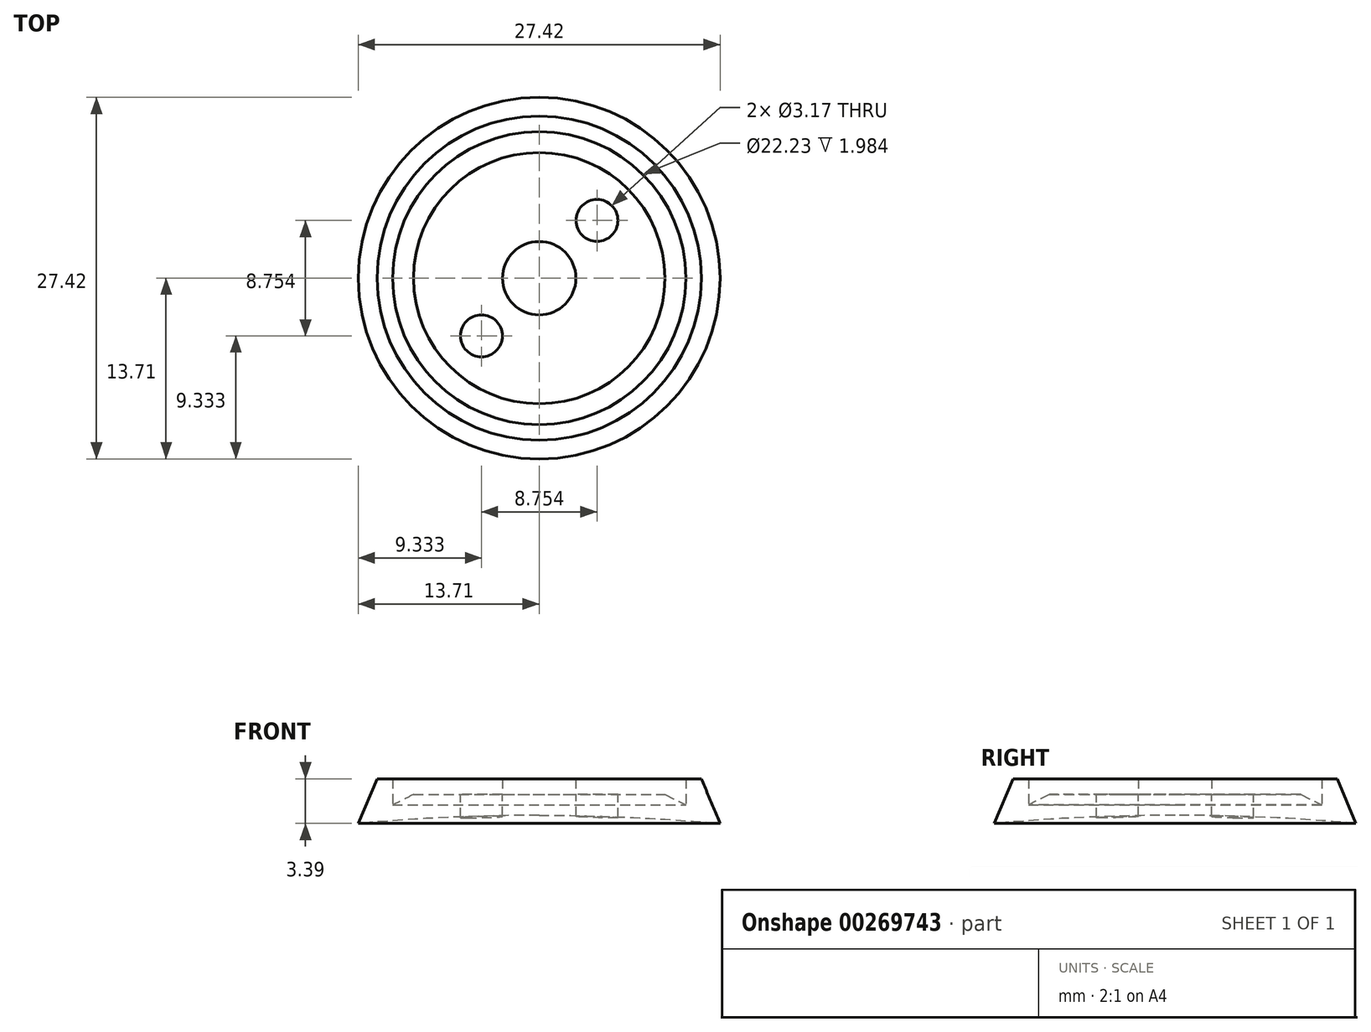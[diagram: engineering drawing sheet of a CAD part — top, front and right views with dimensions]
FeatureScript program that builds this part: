
annotation { "Feature Type Name" : "Feature", "Feature Type Description" : "" }
export const myFeature = defineFeature(function(context is Context, id is Id, definition is map)
    precondition{}
    {
        {
            var Q0;
            Q0=qCreatedBy(makeId("Front.planeOp"),FACE);
            var sketch = newSketch(context, id + "F0", { "sketchPlane" : qUnion([Q0])});
            skArc(sketch, "E0", {"start": v(14.29, 24.73) * mm, "mid": v(7.15, 25.23) * mm, "end": v(0, 25.4) * mm});
            skLineSegment(sketch, "E1", {"start": v(0, 0) * mm, "end": v(0, 65.07) * mm});
            skLineSegment(sketch, "E2", {"start": v(0, 0) * mm, "end": v(11.11, 0) * mm});
            skLineSegment(sketch, "E3", {"start": v(11.11, 0) * mm, "end": v(14.29, 0) * mm});
            skLineSegment(sketch, "E4", {"start": v(14.29, 24.73) * mm, "end": v(14.29, 28.17) * mm});
            skLineSegment(sketch, "E5", {"start": v(14.29, 28.17) * mm, "end": v(11.11, 28.17) * mm});
            skLineSegment(sketch, "E6", {"start": v(2.78, 28.17) * mm, "end": v(0, 28.17) * mm});
            skLineSegment(sketch, "E7", {"start": v(2.78, 28.17) * mm, "end": v(2.78, 26.98) * mm});
            skPoint(sketch, "E8.orphan", {"position": v(11.11, 25) * mm});
            skLineSegment(sketch, "E9", {"start": v(11.11, 26.58) * mm, "end": v(11.11, 28.17) * mm});
            skLineSegment(sketch, "E10", {"start": v(2.78, 26.98) * mm, "end": v(9.53, 26.98) * mm});
            skPoint(sketch, "E11.endSnap0", {"position": v(11.11, 26.58) * mm});
            skLineSegment(sketch, "E12", {"start": v(11.11, 26.58) * mm, "end": v(11.11, 26.18) * mm});
            skPoint(sketch, "E11.start.orphan", {"position": v(11.11, 26.58) * mm});
            skPoint(sketch, "E13", {"position": v(9.53, 26.98) * mm});
            skLineSegment(sketch, "E14", {"start": v(9.53, 26.98) * mm, "end": v(11.11, 26.18) * mm});
            skPoint(sketch, "E15.orphan", {"position": v(11.11, 25.79) * mm});
            skPoint(sketch, "E16.end.orphan", {"position": v(2.78, 26.18) * mm});
            skSolve(sketch);
        }
        {
            var Q0;
            Q0 = qSketchRegion(id + "F0", true);
            var Q1;
            Q1=sQuery(id+"F0.wireOp",EDGE,"E1");
            revolve(context, id + "F1", {"entities" : qUnion([Q0]), "axis" : qUnion([Q1]), "revolveType" : RevolveType.FULL});
        }
        {
            var Q0;
            Q0=makeQuery(id+"F1.opRevolve","SWEPT_EDGE",EDGE,{"disambiguationData":[OSD([sQuery(id+"F0.wireOp",EDGE,"E4"),sQuery(id+"F0.wireOp",EDGE,"E5")])]});
            chamfer(context, id + "F2", {"entities" : qUnion([Q0]), "chamferType" : ChamferType.TWO_OFFSETS, "width1" : 4.76 * mm, "oppositeDirection" : false, "width2" : 2 * mm, "tangentPropagation" : true});
        }
        {
            var Q0;
            Q0=makeQuery(id+"F1.opRevolve","SWEPT_FACE",FACE,{"disambiguationData":[OSD([sQuery(id+"F0.wireOp",EDGE,"E10")])]});
            var sketch = newSketch(context, id + "F3", { "sketchPlane" : qUnion([Q0])});
            skArc(sketch, "E17", {"start": v(-2.86, 0) * mm, "mid": v(1.1, -2.64) * mm, "end": v(2.02, 2.02) * mm});
            skLineSegment(sketch, "E18", {"start": v(0, 0) * mm, "end": v(-9.53, 0) * mm});
            skLineSegment(sketch, "E19", {"start": v(-6.74, -6.74) * mm, "end": v(-2.02, -2.02) * mm});
            skLineSegment(sketch, "E20", {"start": v(2.02, 2.02) * mm, "end": v(6.74, 6.74) * mm});
            skCircle(sketch, "E21", {"center": v(4.38, 4.38) * mm, "radius": 1.59 * mm});
            skCircle(sketch, "E22", {"center": v(-4.38, -4.38) * mm, "radius": 1.59 * mm});
            skSolve(sketch);
        }
        {
            var Q0;
            Q0 = qSketchRegion(id + "F3", true);
            extrude(context, id + "F4", {"entities" : qUnion([Q0]), "operationType" : NewBodyOperationType.REMOVE, "endBound" : BoundingType.THROUGH_ALL, "oppositeDirection" : true, "depth" : 25.4 * mm});
        }
    });
